# Revit family: Danfoss Ally Radiator Thermostat_RFA
name_source: partatom
category: Pipe Accessories
units: mm (PartAtom-declared; Revit-internal decimal feet)

## family parameters
Always vertical = Yes
Cut with Voids When Loaded = No
Part Type = Normal
Round Connector Dimension = Use Diameter
Shared = Yes
Work Plane-Based = No

## types (3) — shared parameters
Actuator = Electromechanical
Adapter_M30 = Yes
Adapter_RA = Yes
Ambient Temperature Range = 0 to 40 °C
Control = PID
D = 55 mm
D1 = 52 mm
Description = Danfoss Ally Radiator Thermostat
Display = LCD with white backlight
H = 77 mm
H1 = 8 mm  [stored 0.0262467 ft]
H2 = 35 mm
H_CALEFFI = 82 mm
H_GIACOMINI = 89 mm
H_M30 = 81 mm
H_RA = 93 mm
H_RAV = 85 mm
H_RAVL = 85 mm
IP Rating = IP20
IfcExportAs = IfcActuatorType
IfcExportType = Danfoss Ally Radiator Thermostat
Manufacturer = Danfoss
Maximum Water Temperature = 90 °C
Model Type = Programmable electronic radiator valve controller
Power Supply = 2 x 1.5 V alkaline AA batteries
Recommended use = Residential (pollution degree 2)
Setting Temperature Range = 5 to 35 °C
Spindle movement = Linear, up to 4.5 mm, max. 2 mm on valve (1 mm/s
URL = https://assets.danfoss.com

## per-type parameters (varying)
| type | Adapter_Caleffi | Adapter_Giacomini | Adapter_RAV | Adapter_RAVL | Model |
| Danfoss Ally Radiator Thermostat_014G2420 | No | No | No | No | 014G2420 |
| Danfoss Ally Radiator Thermostat_014G2460 | No | No | Yes | Yes | 014G2460 |
| Danfoss Ally Radiator Thermostat_014G2461 | Yes | Yes | No | No | 014G2420, 014G2460, 014G2461 |

note: [stored X ft] marks values corroborated as IEEE doubles in the binary element streams (Revit-internal decimal feet)

## geometry (parser evidence)
native form markers: Sweep x15
no freeform markers — native parametric forms only
